# Revit family: Furniture-Floor_Mount-Vanity-KOHLER-Alouette-K-33294
name_source: partatom
category: Plumbing Fixtures
units: mm (PartAtom-declared; Revit-internal decimal feet)

## family parameters
Cut with Voids When Loaded = No
Host = Face
OmniClass Number = 23.21.19.15
OmniClass Title = Specialty Casework
Part Type = Normal
Room Calculation Point = No
Round Connector Dimension = Use Diameter
Shared = No

## types (2) — shared parameters
ADA Compliant = No
Apparent Load = 1440 VA
Assembly Code = D2010400
CW Connection = No
Cold Water Inlet = Cold Water Inlet
Date Modified = 12/20/2024
Default Elevation = 0"
Description = 72 Inch Vanity Set
Drain Included = No
Electrical Connector = Yes
Electrical Note = One Dedicated Electrical Circuit Required
HW Connection = No
Height = 39 3/16"
Hot Water Inlet = Hot Water Inlet
Length = 22 7/16"
Manufacturer = Kohler Co.
Master Format 2014 = 22 41 16
Master Format 2014 Name = Residential Lavatories and Sinks
Material = Solid Wood Construction
Product Documentation Link = https://www.us.kohler.com
Product Name = Alouette
Product Page URL = http://www.us.kohler.com
URL = https://www.us.kohler.com
Vent Connection = No
Voltage = 120 V
Waste Connection = Yes
Waste Water Outlet 1 = Waste Water Outlet 1
Waste Water Outlet 2 = Waste Water Outlet 2
WaterSense Certified = No
Width = 73"

## per-type parameters (varying)
| type | Finish | Model | Type |
| DWG-Warm Dark Grey | KOHLER-Wood-DWG-Warm_Dark_Grey | K-33294-DWG | 1 |
| WEK-Weathered Oak | KOHLER-Wood-WEK-Weathered_Oak | K-33294-WEK | 2 |

## geometry (parser evidence)
native form markers: Sweep x6
no freeform markers — native parametric forms only
